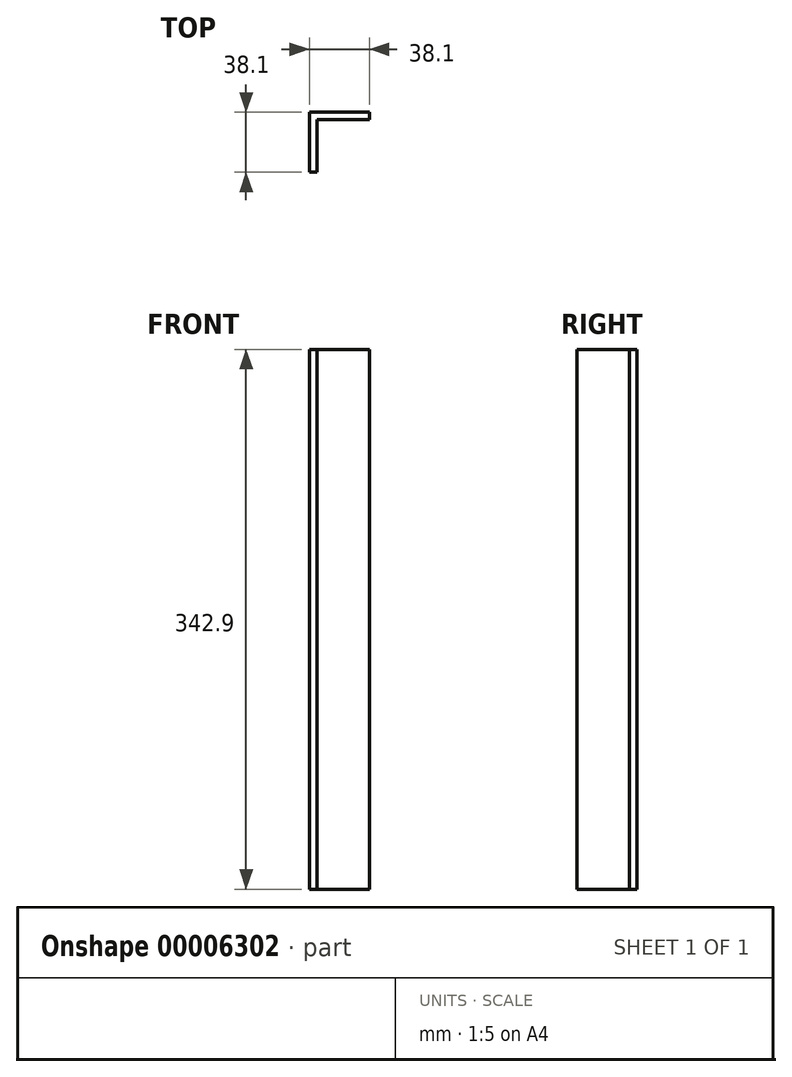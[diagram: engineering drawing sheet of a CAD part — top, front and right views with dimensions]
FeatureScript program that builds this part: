
annotation { "Feature Type Name" : "Feature", "Feature Type Description" : "" }
export const myFeature = defineFeature(function(context is Context, id is Id, definition is map)
    precondition{}
    {
        {
            var Q0;
            Q0=qCreatedBy(makeId("Top.planeOp"),FACE);
            var sketch = newSketch(context, id + "F0", { "sketchPlane" : qUnion([Q0])});
            skLineSegment(sketch, "E0", {"start": v(0, 0) * mm, "end": v(0, -38.1) * mm});
            skLineSegment(sketch, "E1", {"start": v(0, -38.1) * mm, "end": v(4.76, -38.1) * mm});
            skLineSegment(sketch, "E2", {"start": v(4.76, -38.1) * mm, "end": v(4.76, -4.76) * mm});
            skLineSegment(sketch, "E3", {"start": v(4.76, -4.76) * mm, "end": v(38.1, -4.76) * mm});
            skLineSegment(sketch, "E4", {"start": v(38.1, -4.76) * mm, "end": v(38.1, 0) * mm});
            skLineSegment(sketch, "E5", {"start": v(38.1, 0) * mm, "end": v(0, 0) * mm});
            skSolve(sketch);
        }
        {
            var Q0;
            Q0=makeQuery(id+"F0.imprint","IMPRINT",FACE,{"disambiguationData":[TD([[makeQuery(id+"F0.imprint","IMPRINT",EDGE,{"derivedFrom":sQuery(id+"F0.wireOp",EDGE,"E0")}),1.0]])]});
            extrude(context, id + "F1", {"entities" : qUnion([Q0]), "depth" : 342.9 * mm});
        }
    });
